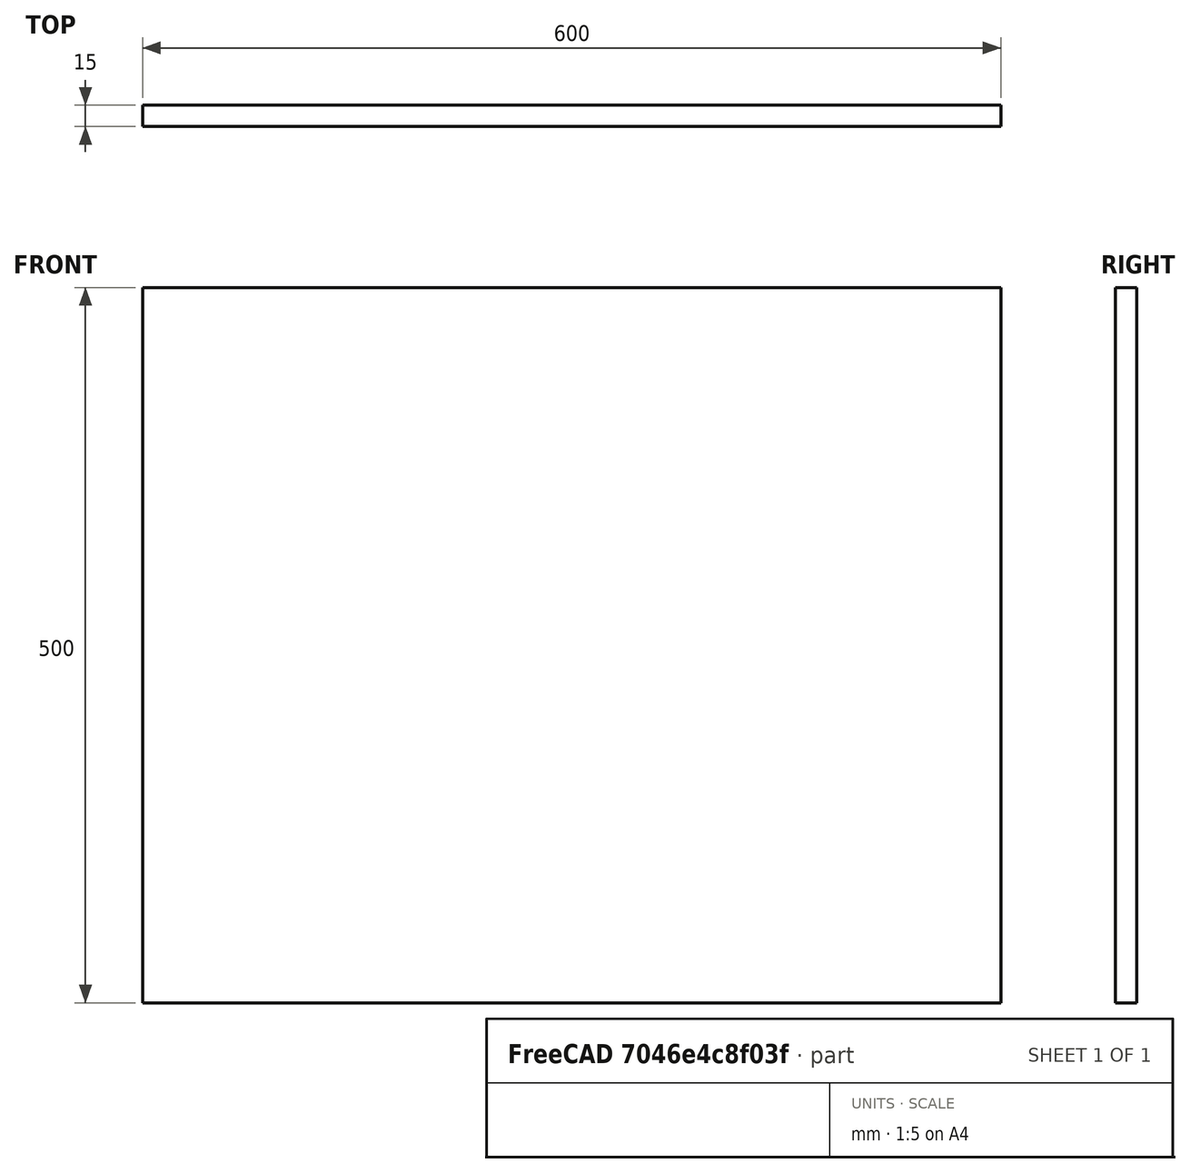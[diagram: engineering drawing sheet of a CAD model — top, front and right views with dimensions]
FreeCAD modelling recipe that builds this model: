
FCSTD DOCUMENT  (FreeCAD 1.0R39319 (Git))
Label: internal_separator
License: All rights reserved
LicenseURL: https://en.wikipedia.org/wiki/All_rights_reserved
objects: Sketcher::SketchObject×1, PartDesign::Pad×1, PartDesign::Body×1
note: 6 computed .brp shape members not serialized (recipe doc carries the construction recipe); baked Part::Feature solids carry a one-line shape summary decoded from their .brp

FEATURE [Sketcher::SketchObject] Sketch  label="internal_separator_s"
  ArcFitTolerance = 1e-06
  AttachmentSupport = -> [XZ_Plane]
  FullyConstrained = true
  MakeInternals = false
  MapMode = 5
  Placement = pos=(0,0,0) rot=(1,0,0;1.5708rad)
  sketch-geometry (4):
    g0: LineSegment StartX=0 StartY=0 StartZ=0 EndX=600 EndY=0 EndZ=0
    g1: LineSegment StartX=600 StartY=0 StartZ=0 EndX=600 EndY=500 EndZ=0
    g2: LineSegment StartX=600 StartY=500 StartZ=0 EndX=0 EndY=500 EndZ=0
    g3: LineSegment StartX=0 StartY=500 StartZ=0 EndX=0 EndY=0 EndZ=0
  constraints (11):
    c: Coincident(g0,g1)
    c: Coincident(g1,g2)
    c: Coincident(g2,g3)
    c: Coincident(g3,g0)
    c: Horizontal(g0)
    c: Horizontal(g2)
    c: Vertical(g1)
    c: Vertical(g3)
    c: Coincident(g0,g-1)
    c: DistanceX(g2,g2) = 600
    c: DistanceY(g3,g3) = 500
FEATURE [PartDesign::Pad] Pad  label="internal_separator"
  Direction = (0,-1,2e-16)
  Length = 15
  Length2 = 10
  Placement = pos=(0,0,0) rot=(1,0,0;1.5708rad)
  Profile = -> Sketch
  ReferenceAxis = -> Sketch [N_Axis]
  Refine = true
  Suppressed = false
  Type = 0
FEATURE [PartDesign::Body] Body  label="internal_separator_body"
  AllowCompound = false
  Group = -> [Sketch,Pad]
  Origin = -> Origin
  Tip = -> Pad
